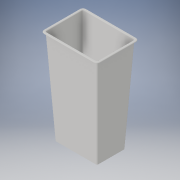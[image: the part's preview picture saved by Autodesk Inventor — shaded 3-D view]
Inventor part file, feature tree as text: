
AUTODESK INVENTOR PART (.ipt)
format: ipt  version: 2017 (Build 210142000, 142)  size: 207,360 bytes
history: native  units: in
note: dims shown in document units (in); Inventor stores cm internally (conversion verified against a paired STEP export)
features: sketch x3, loft x2, extrude x1, plane x1, sweep x1
ambient origin geometry x8: Origin, YZ Plane, XZ Plane, XY Plane, X Axis, Y Axis, Z Axis, Center Point
bodies: Solid1 (feature_tree)
feature tree (8):
  sketch  "Sketch1"  dims[d2=0.0093in d3=0.0093in]
  extrude  "bottom of bin"  Depth=0.0093in
  plane  "Work Plane1"
  sketch  "Sketch2"  dims[d4=0.0093in d6=0.75in]
  loft  "loft make"
  loft  "loft cut"
  sweep  "lip rim"
  sketch  "Sketch3"  dims[d7=1.0in d8=0.0093in d9=0.0in d10=3.3333in d11=0.1667in d12=0.1667in d13=0.1667in d14=0.0093in d15=0.0093in d16=0.0093in d17=0.0364in d18=0.0364in d19=0.0364in d20=0.0in d21=90.0deg d22=0.0in d23=90.0deg d24=0.0in d25=90.0deg d26=0.0in d27=90.0deg d28=0.0833in d29=0.025in d30=0.0in d31=0.0in]
